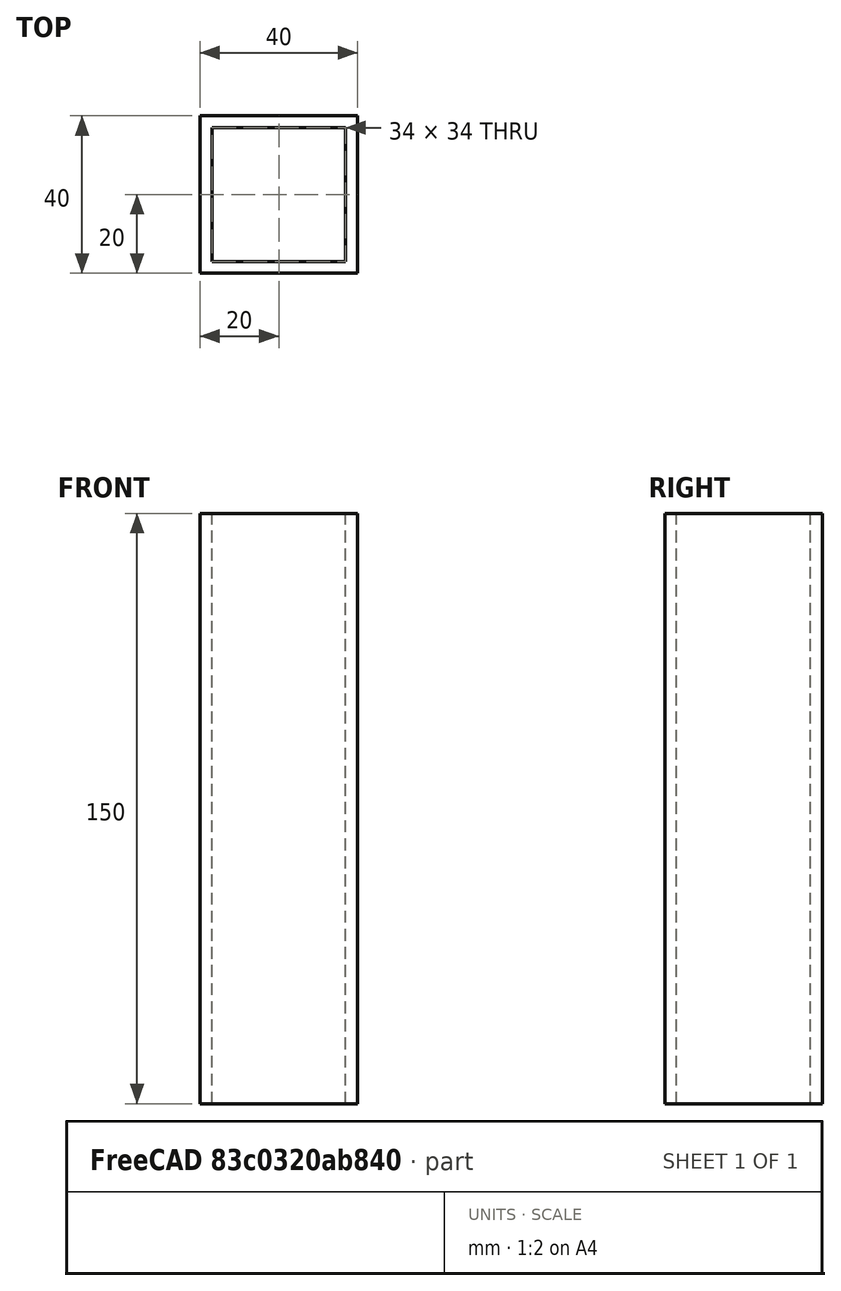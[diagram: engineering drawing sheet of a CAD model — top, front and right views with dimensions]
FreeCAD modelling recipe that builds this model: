
FCSTD DOCUMENT  (FreeCAD 0.21R33771 (Git))
Label: Piedino40x40
License: All rights reserved
LicenseURL: http://en.wikipedia.org/wiki/All_rights_reserved
objects: Sketcher::SketchObject×1, PartDesign::Pad×1, PartDesign::CoordinateSystem×1, PartDesign::Body×1
note: 5 computed .brp shape members not serialized (recipe doc carries the construction recipe); baked Part::Feature solids carry a one-line shape summary decoded from their .brp

FEATURE [Sketcher::SketchObject] Sketch
  FullyConstrained = true
  MapMode = 5
  Support = -> [XY_Plane]
  sketch-geometry (8):
    g0: LineSegment StartX=40 StartY=40 StartZ=0 EndX=0 EndY=40 EndZ=0
    g1: LineSegment StartX=0 StartY=40 StartZ=0 EndX=0 EndY=0 EndZ=0
    g2: LineSegment StartX=0 StartY=0 StartZ=0 EndX=40 EndY=0 EndZ=0
    g3: LineSegment StartX=40 StartY=0 StartZ=0 EndX=40 EndY=40 EndZ=0
    g4: LineSegment StartX=3 StartY=37 StartZ=0 EndX=37 EndY=37 EndZ=0
    g5: LineSegment StartX=37 StartY=37 StartZ=0 EndX=37 EndY=3 EndZ=0
    g6: LineSegment StartX=37 StartY=3 StartZ=0 EndX=3 EndY=3 EndZ=0
    g7: LineSegment StartX=3 StartY=3 StartZ=0 EndX=3 EndY=37 EndZ=0
  constraints (23):
    c: Coincident(g0,g1)
    c: Coincident(g1,g2)
    c: Coincident(g2,g3)
    c: Coincident(g3,g0)
    c: Horizontal(g0)
    c: Horizontal(g2)
    c: Vertical(g1)
    c: Vertical(g3)
    c: Coincident(g1,g-1)
    c: DistanceX(g0,g0) = 40
    c: DistanceY(g1,g1) = 40
    c: Coincident(g4,g5)
    c: Coincident(g5,g6)
    c: Coincident(g6,g7)
    c: Coincident(g7,g4)
    c: Horizontal(g4)
    c: Horizontal(g6)
    c: Vertical(g5)
    c: Vertical(g7)
    c: DistanceX(g6,g6) = 34
    c: DistanceY(g5,g5) = 34
    c: DistanceY(g1,g6) = 3
    c: DistanceX(g1,g6) = 3
FEATURE [PartDesign::Pad] Pad
  Direction = (0,0,1)
  Length = 150
  Length2 = 10
  Profile = -> Sketch
  ReferenceAxis = -> Sketch [N_Axis]
  Type = 0
FEATURE [PartDesign::CoordinateSystem] LCS_piedino40x40
  AttacherType = Attacher::AttachEngine3D
FEATURE [PartDesign::Body] Body  label="Corpo"
  Group = -> [Sketch,Pad,LCS_piedino40x40]
  Origin = -> Origin
  Tip = -> Pad
